# Revit family: 306_R4_
name_source: partatom
category: Pipe Accessories
units: mm (PartAtom-declared; Revit-internal decimal feet)

## family parameters
Always vertical = Yes
Cut with Voids When Loaded = No
Part Type = Valve - Breaks Into
Round Connector Dimension = Use Diameter
Shared = No
Work Plane-Based = No

## types (23) — shared parameters
B1 = 20 mm  [stored 0.0656168 ft]
CAT0 = Yes
Description = Open-close ball valve, 2-way, External thread
G4 = 20 mm  [stored 0.0656168 ft]
H1 = 6 mm  [stored 0.019685 ft]
L2D_Min = 3048 mm
Manufacturer = Belimo
QmdConnectorList = 301;D;302;D
magiPartTypeId = 306
magiProductFamilyId = R4*
zero-valued in all types: MC_Default_elevation

## per-type parameters (varying)
| type | D | G2 | G3 | HH | L1 | L2 | L22 | L22__ve | L2D | LL | LL1 | W2D |
| R405K | 10 mm | 21 mm  [stored 0.0688976 ft] | 19 mm | 26 mm  [stored 0.0853018 ft] | 34 mm  [stored 0.111549 ft] | 13 mm | 6 mm  [stored 0.019685 ft] | -6 mm | 43 mm | 22 mm | 30 mm  [stored 0.0984252 ft] | 10 mm  [stored 0.0328084 ft] |
| R449 | 50 mm | 72 mm | 69 mm | 50 mm | 58 mm | 22 mm | 11 mm | -11 mm | 72 mm | 36 mm  [stored 0.11811 ft] | 50 mm | 50 mm |
| R448 | 50 mm | 72 mm | 69 mm | 50 mm | 58 mm | 22 mm | 11 mm | -11 mm | 72 mm | 36 mm  [stored 0.11811 ft] | 50 mm | 50 mm |
| R439 | 40 mm | 59 mm | 56 mm | 45 mm | 51 mm | 19 mm | 10 mm  [stored 0.0328084 ft] | -10 mm  [stored -0.0328084 ft] | 64 mm | 32 mm  [stored 0.104987 ft] | 45 mm | 40 mm  [stored 0.131234 ft] |
| R438 | 40 mm | 59 mm | 56 mm | 45 mm | 51 mm | 19 mm | 10 mm  [stored 0.0328084 ft] | -10 mm  [stored -0.0328084 ft] | 64 mm | 32 mm  [stored 0.104987 ft] | 45 mm | 40 mm  [stored 0.131234 ft] |
| R431 | 32 mm | 53 mm | 50 mm | 45 mm | 50 mm | 19 mm | 9 mm  [stored 0.0295276 ft] | -9 mm  [stored -0.0295276 ft] | 63 mm | 32 mm  [stored 0.104987 ft] | 44 mm | 32 mm  [stored 0.104987 ft] |
| R429 | 32 mm | 53 mm | 50 mm | 40 mm  [stored 0.131234 ft] | 48 mm  [stored 0.15748 ft] | 18 mm  [stored 0.0590551 ft] | 9 mm  [stored 0.0295276 ft] | -9 mm  [stored -0.0295276 ft] | 60 mm | 30 mm  [stored 0.0984252 ft] | 42 mm  [stored 0.137795 ft] | 32 mm  [stored 0.104987 ft] |
| R424 | 25 mm | 40 mm  [stored 0.131234 ft] | 37 mm | 40 mm  [stored 0.131234 ft] | 42 mm  [stored 0.137795 ft] | 16 mm | 8 mm  [stored 0.0262467 ft] | -8 mm | 52 mm | 26 mm  [stored 0.0853018 ft] | 36 mm  [stored 0.11811 ft] | 25 mm  [stored 0.082021 ft] |
| R423 | 25 mm | 40 mm  [stored 0.131234 ft] | 37 mm | 40 mm  [stored 0.131234 ft] | 42 mm  [stored 0.137795 ft] | 16 mm | 8 mm  [stored 0.0262467 ft] | -8 mm | 52 mm | 26 mm  [stored 0.0853018 ft] | 36 mm  [stored 0.11811 ft] | 25 mm  [stored 0.082021 ft] |
| R422 | 25 mm | 40 mm  [stored 0.131234 ft] | 37 mm | 40 mm  [stored 0.131234 ft] | 42 mm  [stored 0.137795 ft] | 16 mm | 8 mm  [stored 0.0262467 ft] | -8 mm | 52 mm | 26 mm  [stored 0.0853018 ft] | 36 mm  [stored 0.11811 ft] | 25 mm  [stored 0.082021 ft] |
| R419 | 20 mm | 34 mm  [stored 0.111549 ft] | 31 mm | 40 mm  [stored 0.131234 ft] | 42 mm  [stored 0.137795 ft] | 16 mm | 8 mm  [stored 0.0262467 ft] | -8 mm | 53 mm | 27 mm  [stored 0.0885827 ft] | 37 mm | 20 mm  [stored 0.0656168 ft] |
| R418 | 20 mm | 34 mm  [stored 0.111549 ft] | 31 mm | 40 mm  [stored 0.131234 ft] | 42 mm  [stored 0.137795 ft] | 16 mm | 8 mm  [stored 0.0262467 ft] | -8 mm | 53 mm | 27 mm  [stored 0.0885827 ft] | 37 mm | 20 mm  [stored 0.0656168 ft] |
| R417 | 20 mm | 34 mm  [stored 0.111549 ft] | 31 mm | 40 mm  [stored 0.131234 ft] | 42 mm  [stored 0.137795 ft] | 16 mm | 8 mm  [stored 0.0262467 ft] | -8 mm | 53 mm | 27 mm  [stored 0.0885827 ft] | 37 mm | 20 mm  [stored 0.0656168 ft] |
| R414 | 15 mm | 27 mm  [stored 0.0885827 ft] | 25 mm  [stored 0.082021 ft] | 38 mm  [stored 0.124672 ft] | 37 mm | 14 mm  [stored 0.0459318 ft] | 7 mm  [stored 0.0229659 ft] | -7 mm | 46 mm | 23 mm  [stored 0.0754593 ft] | 32 mm  [stored 0.104987 ft] | 15 mm  [stored 0.0492126 ft] |
| R413 | 15 mm | 27 mm  [stored 0.0885827 ft] | 25 mm  [stored 0.082021 ft] | 38 mm  [stored 0.124672 ft] | 37 mm | 14 mm  [stored 0.0459318 ft] | 7 mm  [stored 0.0229659 ft] | -7 mm | 46 mm | 23 mm  [stored 0.0754593 ft] | 32 mm  [stored 0.104987 ft] | 15 mm  [stored 0.0492126 ft] |
| R412 | 15 mm | 27 mm  [stored 0.0885827 ft] | 25 mm  [stored 0.082021 ft] | 38 mm  [stored 0.124672 ft] | 37 mm | 14 mm  [stored 0.0459318 ft] | 7 mm  [stored 0.0229659 ft] | -7 mm | 46 mm | 23 mm  [stored 0.0754593 ft] | 32 mm  [stored 0.104987 ft] | 15 mm  [stored 0.0492126 ft] |
| R411 | 15 mm | 27 mm  [stored 0.0885827 ft] | 25 mm  [stored 0.082021 ft] | 38 mm  [stored 0.124672 ft] | 37 mm | 14 mm  [stored 0.0459318 ft] | 7 mm  [stored 0.0229659 ft] | -7 mm | 46 mm | 23 mm  [stored 0.0754593 ft] | 32 mm  [stored 0.104987 ft] | 15 mm  [stored 0.0492126 ft] |
| R410 | 15 mm | 27 mm  [stored 0.0885827 ft] | 25 mm  [stored 0.082021 ft] | 38 mm  [stored 0.124672 ft] | 37 mm | 14 mm  [stored 0.0459318 ft] | 7 mm  [stored 0.0229659 ft] | -7 mm | 46 mm | 23 mm  [stored 0.0754593 ft] | 32 mm  [stored 0.104987 ft] | 15 mm  [stored 0.0492126 ft] |
| R409 | 15 mm | 27 mm  [stored 0.0885827 ft] | 25 mm  [stored 0.082021 ft] | 38 mm  [stored 0.124672 ft] | 37 mm | 14 mm  [stored 0.0459318 ft] | 7 mm  [stored 0.0229659 ft] | -7 mm | 46 mm | 23 mm  [stored 0.0754593 ft] | 32 mm  [stored 0.104987 ft] | 15 mm  [stored 0.0492126 ft] |
| R409K | 10 mm | 21 mm  [stored 0.0688976 ft] | 19 mm | 26 mm  [stored 0.0853018 ft] | 34 mm  [stored 0.111549 ft] | 13 mm | 6 mm  [stored 0.019685 ft] | -6 mm | 43 mm | 22 mm | 30 mm  [stored 0.0984252 ft] | 10 mm  [stored 0.0328084 ft] |
| R408K | 10 mm | 21 mm  [stored 0.0688976 ft] | 19 mm | 26 mm  [stored 0.0853018 ft] | 34 mm  [stored 0.111549 ft] | 13 mm | 6 mm  [stored 0.019685 ft] | -6 mm | 43 mm | 22 mm | 30 mm  [stored 0.0984252 ft] | 10 mm  [stored 0.0328084 ft] |
| R407K | 10 mm | 21 mm  [stored 0.0688976 ft] | 19 mm | 26 mm  [stored 0.0853018 ft] | 34 mm  [stored 0.111549 ft] | 13 mm | 6 mm  [stored 0.019685 ft] | -6 mm | 43 mm | 22 mm | 30 mm  [stored 0.0984252 ft] | 10 mm  [stored 0.0328084 ft] |
| R406K | 10 mm | 21 mm  [stored 0.0688976 ft] | 19 mm | 26 mm  [stored 0.0853018 ft] | 34 mm  [stored 0.111549 ft] | 13 mm | 6 mm  [stored 0.019685 ft] | -6 mm | 43 mm | 22 mm | 30 mm  [stored 0.0984252 ft] | 10 mm  [stored 0.0328084 ft] |

note: column(s) folded — value = type name in every type: magiProductCode, magiProductId

note: [stored X ft] marks values corroborated as IEEE doubles in the binary element streams (Revit-internal decimal feet)

## geometry (parser evidence)
native form markers: Sweep x1
no freeform markers — native parametric forms only
